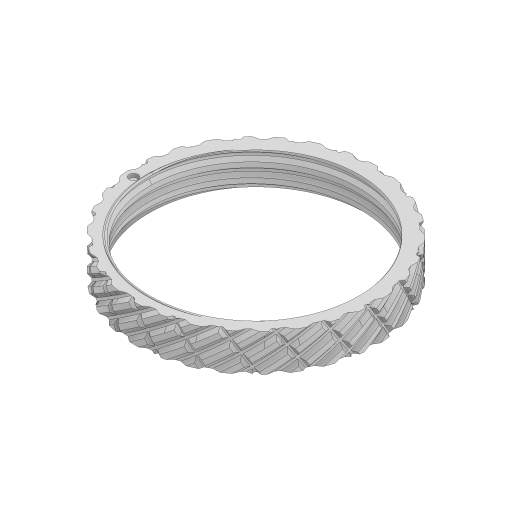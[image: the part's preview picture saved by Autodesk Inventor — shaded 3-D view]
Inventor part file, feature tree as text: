
AUTODESK INVENTOR PART (.ipt)
format: ipt  version: 2023 (Build 270158000, 158)  size: 1,629,184 bytes
history: native  units: mm
features: helix x6, sketch x3, pattern_circular x2, revolve x1, hole x1, direct_edit x1, other x1
ambient origin geometry x8: Origin, YZ Plane, XZ Plane, XY Plane, X Axis, Y Axis, Z Axis, Center Point
bodies: Solid1 (feature_tree)
feature tree (15):
  sketch  "Sketch1"  dims[d0=12.7mm d1=1.2mm d2=16.755161mm d3=12.875mm d4=2.2mm d5=5.0mm d6=90.0deg d7=2.0mm d8=5.0mm d9=10.0mm d10=-1.047198mm]
  revolve  "Revolution1"  [1 undecoded]
  helix  "Coil1"  [1 undecoded]
  helix  "Coil2"  [1 undecoded]
  sketch  "Sketch3"  dims[d11=90.0deg d12=90.0deg d13=0.0mm d14=0.0mm]
  helix  "Coil3"  [1 undecoded]
  helix  "Coil4"  [1 undecoded]
  pattern_circular  "Circular Pattern1"  [2 undecoded]
  helix  "Coil5"  [1 undecoded]
  helix  "Coil6"  [1 undecoded]
  pattern_circular  "Circular Pattern2"  [2 undecoded]
  hole  "Hole1"  [1 undecoded]
  direct_edit  "Direct Edit1"
  sketch  "Sketch4"  dims[d15=2.0mm d16=5.0mm d17=10.0mm d18=1.047198mm d19=90.0deg d20=90.0deg d21=0.0mm d22=0.0mm d37=0.5mm d39=0.5mm d41=1.5mm d42=6.981317mm d43=6.981317mm d44=0.707706mm d45=0.707706mm d46=70.0mm d47=10.0mm d48=10.0mm d49=0.0mm d50=90.0deg d51=90.0deg d52=0.0mm d53=0.0mm d54=70.0mm d55=10.0mm d56=10.0mm d57=0.0mm d58=90.0deg d59=90.0deg d60=0.0mm d61=0.0mm d62=300.0mm d63=360.0deg d65=150.0mm d66=10.0mm d67=10.0mm d68=0.0mm d69=90.0deg d70=90.0deg d71=0.0mm d72=0.0mm d73=150.0mm d74=10.0mm d75=10.0mm d76=0.0mm d77=90.0deg d78=90.0deg d79=0.0mm d80=0.0mm d81=200.0mm d82=360.0deg d84=1.2mm d85=6.0mm d86=4.0mm d87=2.0mm d88=90.0deg d89=0.5mm d90=0.0mm d91=-0.254mm d92=14.660766mm]
  other  "Size1"
note: 12 required parameter values undecoded (feature->parameter linkage not recoverable at this tier; creation-order binding heuristic only, values carry confidence <= 0.55)